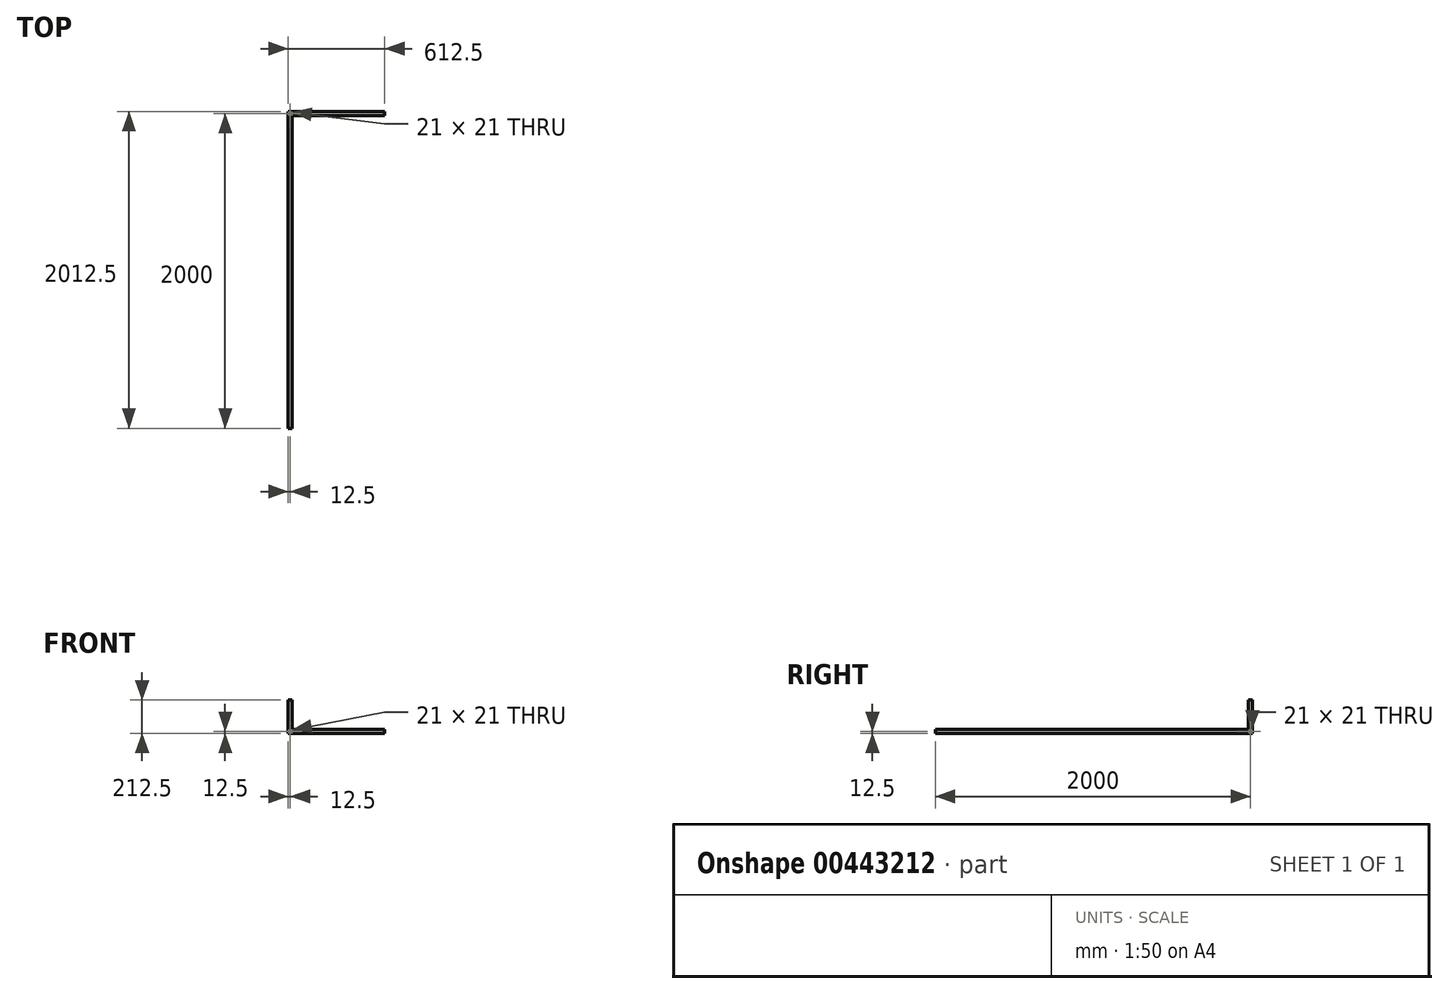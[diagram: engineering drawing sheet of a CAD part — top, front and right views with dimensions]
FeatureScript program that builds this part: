
annotation { "Feature Type Name" : "Feature", "Feature Type Description" : "" }
export const myFeature = defineFeature(function(context is Context, id is Id, definition is map)
    precondition{}
    {
        {
            var Q0;
            Q0=qCreatedBy(makeId("Front.planeOp"),FACE);
            var sketch = newSketch(context, id + "F0", { "sketchPlane" : qUnion([Q0])});
            skLineSegment(sketch, "E0.bottom", {"start": v(-10.5, -10.5) * mm, "end": v(10.5, -10.5) * mm});
            skLineSegment(sketch, "E0.top", {"start": v(-10.5, 10.5) * mm, "end": v(10.5, 10.5) * mm});
            skLineSegment(sketch, "E0.left", {"start": v(-10.5, -10.5) * mm, "end": v(-10.5, 10.5) * mm});
            skLineSegment(sketch, "E0.right", {"start": v(10.5, -10.5) * mm, "end": v(10.5, 10.5) * mm});
            skPoint(sketch, "E0.middle", {"position": v(0, 0) * mm});
            skLineSegment(sketch, "E1.bottom", {"start": v(-12.5, 12.5) * mm, "end": v(12.5, 12.5) * mm});
            skLineSegment(sketch, "E1.top", {"start": v(-12.5, -12.5) * mm, "end": v(12.5, -12.5) * mm});
            skLineSegment(sketch, "E1.left", {"start": v(-12.5, 12.5) * mm, "end": v(-12.5, -12.5) * mm});
            skLineSegment(sketch, "E1.right", {"start": v(12.5, 12.5) * mm, "end": v(12.5, -12.5) * mm});
            skSolve(sketch);
        }
        {
            var Q0;
            Q0 = qSketchRegion(id + "F0", true);
            extrude(context, id + "F1", {"entities" : qUnion([Q0]), "depth" : 2000 * mm});
        }
        {
            var Q0;
            Q0=qCreatedBy(makeId("Right.planeOp"),FACE);
            var sketch = newSketch(context, id + "F2", { "sketchPlane" : qUnion([Q0])});
            skLineSegment(sketch, "E2.bottom", {"start": v(10.5, 10.5) * mm, "end": v(-10.5, 10.5) * mm});
            skLineSegment(sketch, "E2.top", {"start": v(10.5, -10.5) * mm, "end": v(-10.5, -10.5) * mm});
            skLineSegment(sketch, "E2.left", {"start": v(10.5, 10.5) * mm, "end": v(10.5, -10.5) * mm});
            skLineSegment(sketch, "E2.right", {"start": v(-10.5, 10.5) * mm, "end": v(-10.5, -10.5) * mm});
            skPoint(sketch, "E2.middle", {"position": v(0, 0) * mm});
            skLineSegment(sketch, "E3.bottom", {"start": v(12.5, 12.5) * mm, "end": v(-12.5, 12.5) * mm});
            skLineSegment(sketch, "E3.top", {"start": v(12.5, -12.5) * mm, "end": v(-12.5, -12.5) * mm});
            skLineSegment(sketch, "E3.left", {"start": v(12.5, 12.5) * mm, "end": v(12.5, -12.5) * mm});
            skLineSegment(sketch, "E3.right", {"start": v(-12.5, 12.5) * mm, "end": v(-12.5, -12.5) * mm});
            skSolve(sketch);
        }
        {
            var Q0;
            Q0 = qSketchRegion(id + "F2", true);
            extrude(context, id + "F3", {"entities" : qUnion([Q0]), "depth" : 600 * mm});
        }
        {
            var Q0;
            Q0=qCreatedBy(makeId("Top.planeOp"),FACE);
            var sketch = newSketch(context, id + "F4", { "sketchPlane" : qUnion([Q0])});
            skLineSegment(sketch, "E4.bottom", {"start": v(-10.5, 10.5) * mm, "end": v(10.5, 10.5) * mm});
            skLineSegment(sketch, "E4.top", {"start": v(-10.5, -10.5) * mm, "end": v(10.5, -10.5) * mm});
            skLineSegment(sketch, "E4.left", {"start": v(-10.5, 10.5) * mm, "end": v(-10.5, -10.5) * mm});
            skLineSegment(sketch, "E4.right", {"start": v(10.5, 10.5) * mm, "end": v(10.5, -10.5) * mm});
            skPoint(sketch, "E4.middle", {"position": v(0, 0) * mm});
            skLineSegment(sketch, "E5.bottom", {"start": v(-12.5, 12.5) * mm, "end": v(12.5, 12.5) * mm});
            skLineSegment(sketch, "E5.top", {"start": v(-12.5, -12.5) * mm, "end": v(12.5, -12.5) * mm});
            skLineSegment(sketch, "E5.left", {"start": v(-12.5, 12.5) * mm, "end": v(-12.5, -12.5) * mm});
            skLineSegment(sketch, "E5.right", {"start": v(12.5, 12.5) * mm, "end": v(12.5, -12.5) * mm});
            skSolve(sketch);
        }
        {
            var Q0;
            Q0 = qSketchRegion(id + "F4", true);
            extrude(context, id + "F5", {"entities" : qUnion([Q0]), "depth" : 200 * mm});
        }
    });
